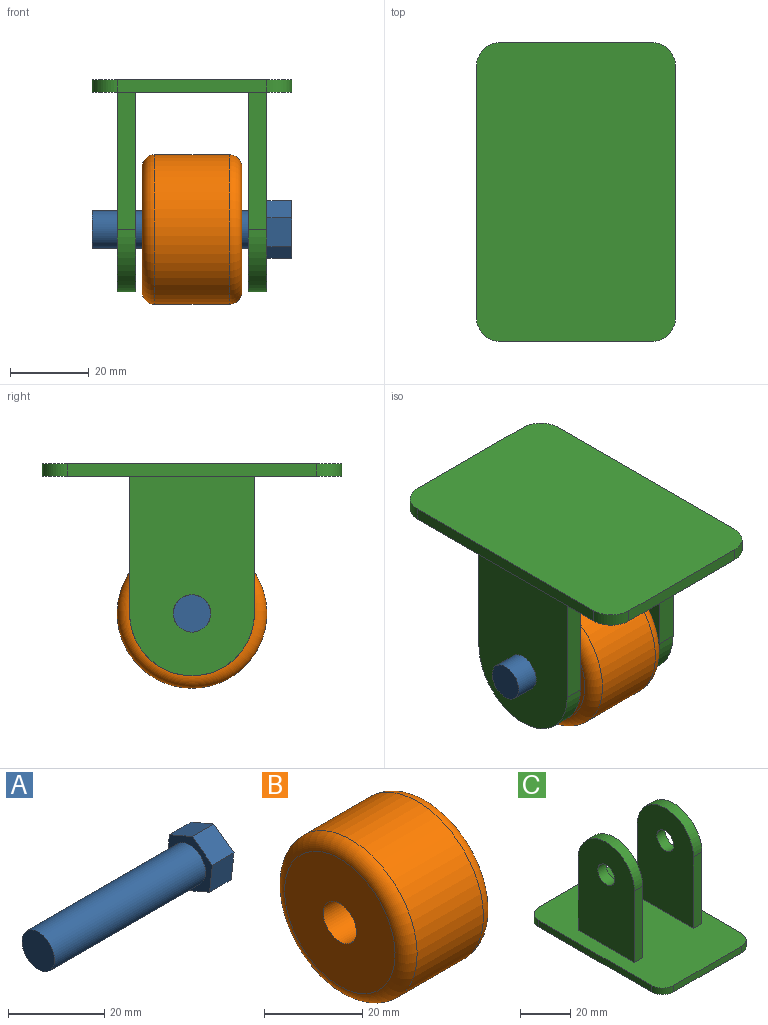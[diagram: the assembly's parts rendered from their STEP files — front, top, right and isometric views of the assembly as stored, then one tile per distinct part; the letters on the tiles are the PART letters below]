
ASSEMBLY  parts=3 mates=2
PART A: 10 faces, bbox 50.8x13.5x14.6 mm
  f0: cylinder r=4.76mm len=44.45mm, axis (-1,0,0), area 1330.1mm2, adj f1,f9
  f1: plane 9.53x9.53mm, normal (-1,0,0), area 71.3mm2, adj f0
  f2: plane 6.73x6.35mm, normal (0,-0.4,-0.92), area 46.6mm2, adj f3,f7,f8,f9
  f3: plane 6.35x5.89mm, normal (0,0.6,-0.8), area 46.6mm2, adj f2,f4,f8,f9
  f4: plane 7.28x6.35mm, normal (0,0.99,0.11), area 46.6mm2, adj f3,f5,f8,f9
  f5: plane 6.73x6.35mm, normal (0,0.4,0.92), area 46.6mm2, adj f4,f6,f8,f9
  f6: plane 6.35x5.89mm, normal (0,-0.6,0.8), area 46.6mm2, adj f5,f7,f8,f9
  f7: plane 7.28x6.35mm, normal (0,-0.99,-0.11), area 46.6mm2, adj f2,f6,f8,f9
  f8: plane 14.57x13.46mm, normal (1,0,0), area 139.7mm2, adj f2,f3,f4,f5,f6,f7
  f9: plane 14.57x13.46mm, normal (-1,0,0), area 68.4mm2, adj f0,f2,f3,f4,f5,f6,f7
PART B: 6 faces, bbox 25.4x41.2x41.2 mm
  f0: cylinder r=4.76mm len=25.4mm, axis (-1,0,0), area 760.1mm2, adj f2,f3
  f1: cylinder r=19.05mm len=38.1mm, axis (-1,0,0), area 2280.2mm2, adj f4,f5
  f2: plane 31.75x31.75mm, normal (1,0,0), area 720.5mm2, adj f0,f5
  f3: plane 31.75x31.75mm, normal (-1,0,0), area 720.5mm2, adj f0,f4
  f4: torus R=15.88mm, axis (1,0,0), area 560.8mm2, adj f1,f3
  f5: torus R=15.88mm, axis (1,0,0), area 560.8mm2, adj f1,f2
PART C: 22 faces, bbox 50.8x76.2x54 mm
  f0: plane 34.93x4.76mm, normal (0,1,0), area 166.3mm2, adj f1,f4,f18,f21
  f1: cylinder r=15.88mm len=31.75mm, axis (-1,0,0), area 237.5mm2, adj f0,f2,f18,f21
  f2: plane 34.93x4.76mm, normal (0,-1,0), area 166.3mm2, adj f1,f4,f18,f21
  f3: cylinder r=4.76mm len=9.53mm, axis (-1,0,0), area 142.5mm2, adj f18,f21
  f4: plane 76.2x50.8mm, normal (0,0,1), area 3533.9mm2, adj f0,f2,f5,f6,f7,f8,f9,f10
  f5: plane 38.1x3.18mm, normal (0,1,0), area 121mm2, adj f4,f6,f12,f13
  f6: cylinder r=6.35mm len=6.35mm, axis (0,0,-1), area 31.7mm2, adj f4,f5,f7,f13
  f7: plane 63.5x3.18mm, normal (-1,0,0), area 201.6mm2, adj f4,f6,f8,f13
  f8: cylinder r=6.35mm len=6.35mm, axis (0,0,-1), area 31.7mm2, adj f4,f7,f9,f13
  f9: plane 38.1x3.18mm, normal (0,-1,0), area 121mm2, adj f4,f8,f10,f13
  f10: cylinder r=6.35mm len=6.35mm, axis (0,0,-1), area 31.7mm2, adj f4,f9,f11,f13
  f11: plane 63.5x3.18mm, normal (1,0,0), area 201.6mm2, adj f4,f10,f12,f13
  f12: cylinder r=6.35mm len=6.35mm, axis (0,0,-1), area 31.7mm2, adj f4,f5,f11,f13
  f13: plane 76.2x50.8mm, normal (0,0,-1), area 3836.3mm2, adj f5,f6,f7,f8,f9,f10,f11,f12
  f14: plane 34.93x4.76mm, normal (0,1,0), area 166.3mm2, adj f4,f15,f19,f20
  f15: cylinder r=15.88mm len=31.75mm, axis (-1,0,0), area 237.5mm2, adj f14,f16,f19,f20
  f16: plane 34.93x4.76mm, normal (0,-1,0), area 166.3mm2, adj f4,f15,f19,f20
  f17: cylinder r=4.76mm len=9.53mm, axis (-1,0,0), area 142.5mm2, adj f19,f20
  f18: plane 50.8x31.75mm, normal (1,0,0), area 1433.5mm2, adj f0,f1,f2,f3,f4
  f19: plane 50.8x31.75mm, normal (-1,0,0), area 1433.5mm2, adj f4,f14,f15,f16,f17
  f20: plane 50.8x31.75mm, normal (1,0,0), area 1433.5mm2, adj f4,f14,f15,f16,f17
  f21: plane 50.8x31.75mm, normal (-1,0,0), area 1433.5mm2, adj f0,f1,f2,f3,f4
PLACE A t=(-25.4,0,0)mm
PLACE B t=(-12.7,0,0)mm
PLACE C rot(axis=(0,1,0),180deg) t=(0,0,38.1)mm
MATE revolute A.f0 <-> C.f1  axis (-1,0,0) through (19.05,0,0)mm
MATE revolute B.f0 <-> A.f0  axis (-1,0,0) through (12.7,0,0)mm
